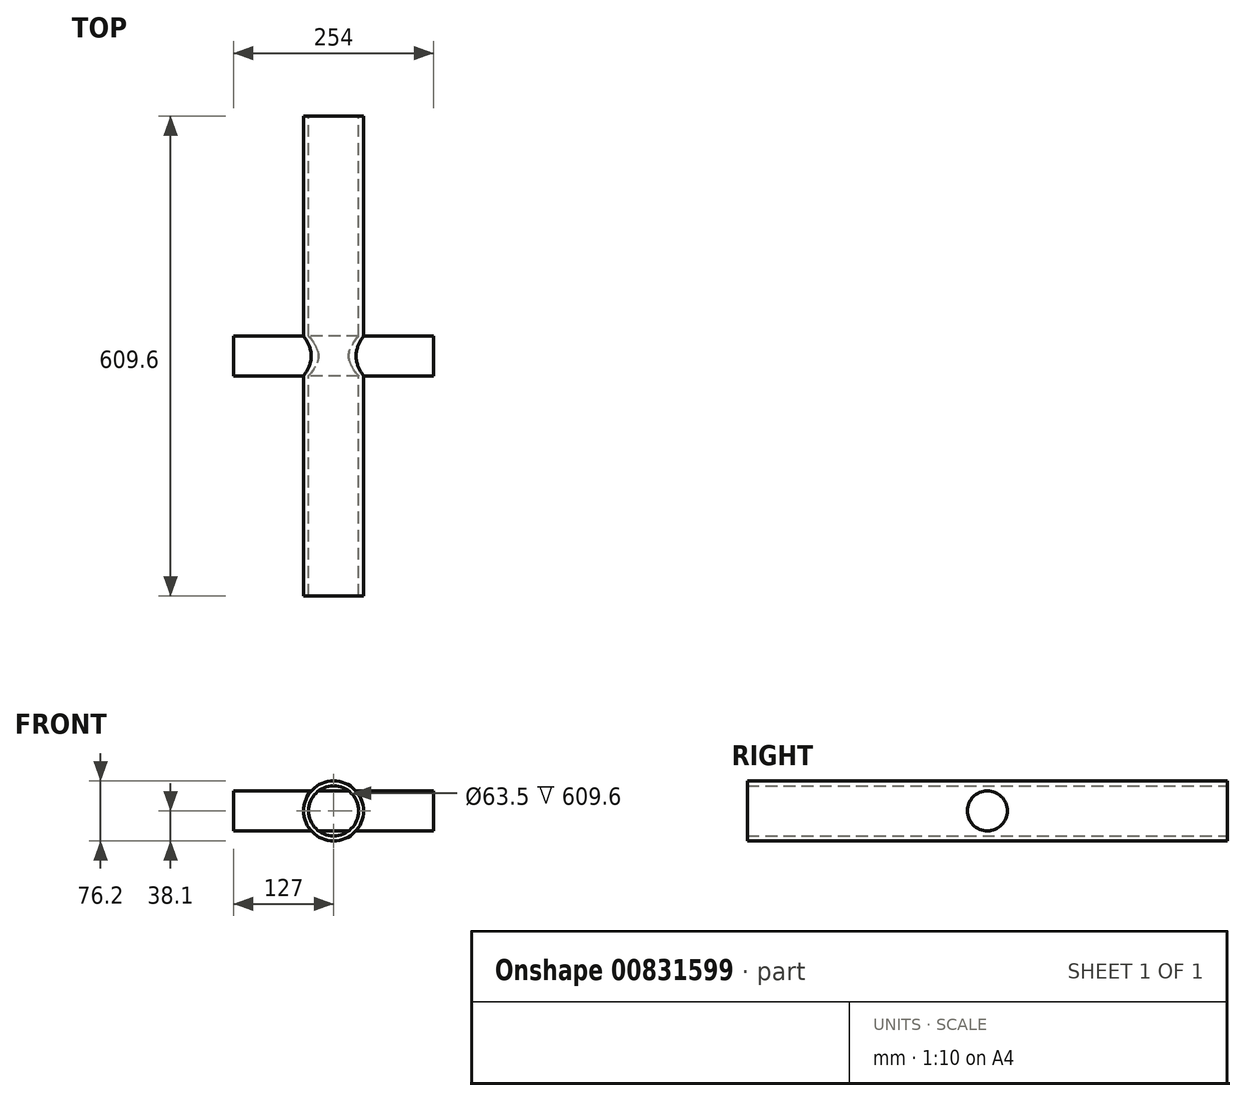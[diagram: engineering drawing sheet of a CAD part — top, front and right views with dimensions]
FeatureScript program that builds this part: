
annotation { "Feature Type Name" : "Feature", "Feature Type Description" : "" }
export const myFeature = defineFeature(function(context is Context, id is Id, definition is map)
    precondition{}
    {
        {
            var Q0;
            Q0=qCreatedBy(makeId("Front.planeOp"),FACE);
            var sketch = newSketch(context, id + "F0", { "sketchPlane" : qUnion([Q0])});
            skCircle(sketch, "E0", {"center": v(0, 0) * mm, "radius": 38.1 * mm});
            skCircle(sketch, "E1", {"center": v(0, 0) * mm, "radius": 31.75 * mm});
            skSolve(sketch);
        }
        {
            var Q0;
            Q0=makeQuery(id+"F0.imprint","IMPRINT",FACE,{"disambiguationData":[TD([[makeQuery(id+"F0.imprint","IMPRINT",EDGE,{"derivedFrom":sQuery(id+"F0.wireOp",EDGE,"E0")}),1.0]])]});
            var Q1;
            Q1=sQuery(id+"F0.wireOp",EDGE,"E0");
            var Q2;
            Q2=sQuery(id+"F0.wireOp",EDGE,"E1");
            extrude(context, id + "F1", {"entities" : qUnion([Q0]), "surfaceEntities" : qUnion([Q1, Q2]), "endBound" : BoundingType.SYMMETRIC, "depth" : 609.6 * mm, "offsetDistance" : 25.4 * mm});
        }
        {
            var Q0;
            Q0=qCreatedBy(makeId("Right.planeOp"),FACE);
            var sketch = newSketch(context, id + "F2", { "sketchPlane" : qUnion([Q0])});
            skCircle(sketch, "E2", {"center": v(0, 0) * mm, "radius": 25.4 * mm});
            skSolve(sketch);
        }
        {
            var Q0;
            Q0 = qSketchRegion(id + "F2", true);
            extrude(context, id + "F3", {"entities" : qUnion([Q0]), "operationType" : NewBodyOperationType.ADD, "endBound" : BoundingType.SYMMETRIC, "depth" : 254 * mm, "offsetDistance" : 25.4 * mm});
        }
    });
